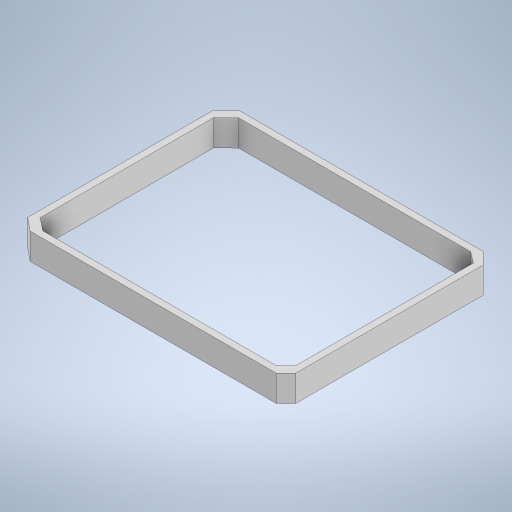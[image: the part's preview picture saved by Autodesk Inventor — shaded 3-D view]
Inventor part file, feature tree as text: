
AUTODESK INVENTOR PART (.ipt)
format: ipt  version: 2024 (Build 280153000, 153)  size: 249,344 bytes
history: native  units: mm
features: extrude x1, sketch x1
ambient origin geometry x8: Origin, YZ Plane, XZ Plane, XY Plane, X Axis, Y Axis, Z Axis, Center Point
bodies: Solid1 (feature_tree)
feature tree (2):
  extrude  "Extrusion1"  Depth=2.0mm
  sketch  "Sketch1"  dims[d1=2.0mm d2=2.0mm d3=2.0mm d4=2.0mm d5=8.0mm d6=0.0mm]
